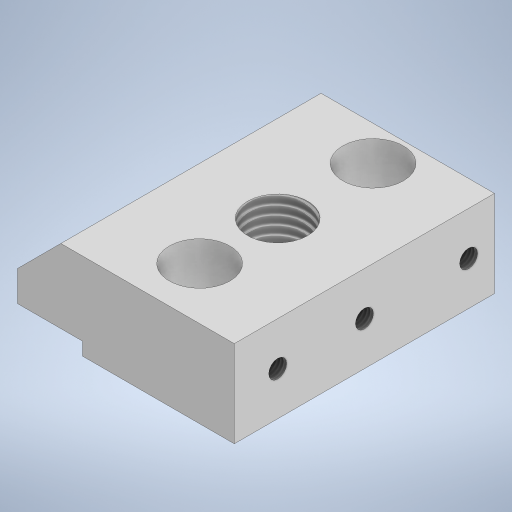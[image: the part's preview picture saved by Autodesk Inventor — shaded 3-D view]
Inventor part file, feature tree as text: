
AUTODESK INVENTOR PART (.ipt)
format: ipt  version: 2024 (Build 280153000, 153)  size: 271,872 bytes
history: native  units: mm
features: hole x6, sketch x6, extrude x1
ambient origin geometry x8: Origin, YZ Plane, XZ Plane, XY Plane, X Axis, Y Axis, Z Axis, Center Point
bodies: Volumenkörper1 (feature_tree)
feature tree (13):
  extrude  "Extrusion1"  Depth=10.0mm
  hole  "Bohrung1"  [1 undecoded]
  sketch  "Skizze3"  dims[d4=40.0mm d5=15.0mm]
  hole  "Bohrung2"  [1 undecoded]
  hole  "Bohrung3"  [1 undecoded]
  hole  "Bohrung4"  [1 undecoded]
  hole  "Bohrung5"  [1 undecoded]
  hole  "Bohrung6"  [1 undecoded]
  sketch  "Skizze1"  dims[d0=10.0mm d1=10.0mm]
  sketch  "Skizze2"  dims[d2=3.0mm d3=20.0mm]
  sketch  "Skizze6"  dims[d6=60.0mm d7=0.0mm d8=7.0mm]
  sketch  "Skizze7"  dims[d9=7.0mm d10=40.0mm]
  sketch  "Skizze8"  dims[d11=10.0mm d12=3.242mm d13=8.0mm d14=4.0mm d15=2.0mm d16=90.0deg d17=12.0mm d18=20.594885mm d19=20.0mm d20=12.0mm d21=40.0mm d22=14.0mm d23=8.0mm d24=4.0mm d25=2.0mm d26=90.0deg d27=8.0mm d28=20.594885mm d29=13.835mm d30=32.0mm d31=4.0mm d32=2.0mm d33=90.0deg d34=8.0mm d35=0.0mm d37=4.134mm d38=10.0mm d39=4.0mm d40=2.0mm d41=90.0deg d42=10.0mm d43=20.594885mm d44=4.134mm d45=10.0mm d46=4.0mm d47=2.0mm d48=90.0deg d49=10.0mm d50=20.594885mm d51=10.0mm d52=4.134mm d53=10.0mm d54=4.0mm d55=2.0mm d56=90.0deg d57=10.0mm d58=20.594885mm d59=30.0mm]
note: 6 required parameter values undecoded (feature->parameter linkage not recoverable at this tier; creation-order binding heuristic only, values carry confidence <= 0.55)
